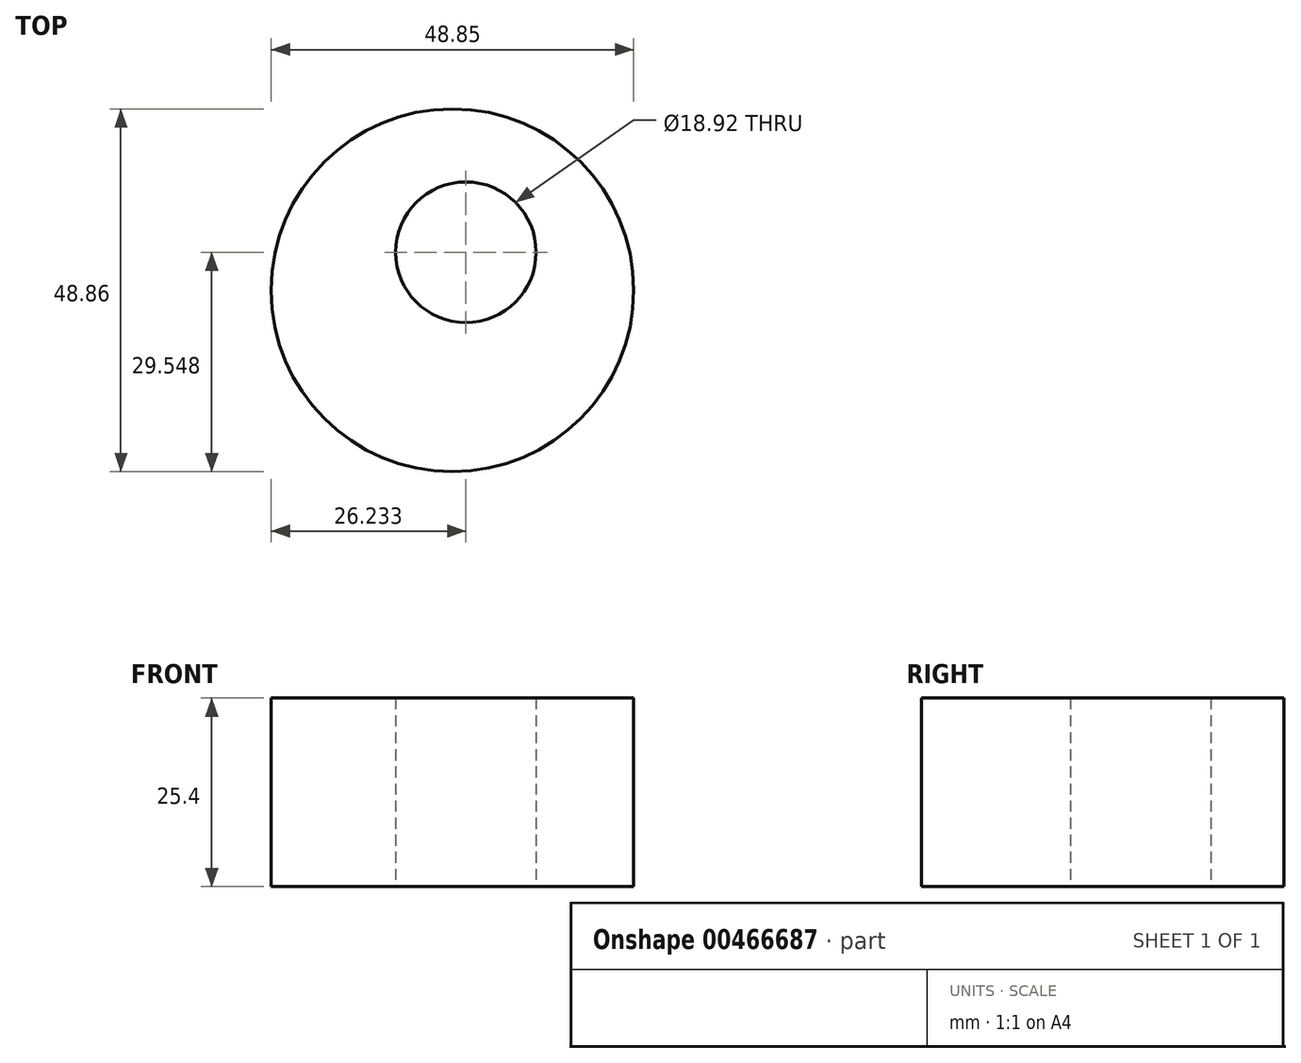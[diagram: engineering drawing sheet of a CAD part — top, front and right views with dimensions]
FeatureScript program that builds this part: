
annotation { "Feature Type Name" : "Feature", "Feature Type Description" : "" }
export const myFeature = defineFeature(function(context is Context, id is Id, definition is map)
    precondition{}
    {
        {
            var Q0;
            Q0=qCreatedBy(makeId("Top.planeOp"),FACE);
            var sketch = newSketch(context, id + "F0", { "sketchPlane" : qUnion([Q0])});
            skCircle(sketch, "E0", {"center": v(-11.27, 16.87) * mm, "radius": 24.43 * mm});
            skCircle(sketch, "E1", {"center": v(-9.47, 21.99) * mm, "radius": 9.46 * mm});
            skSolve(sketch);
        }
        {
            var Q0;
            Q0=makeQuery(id+"F0.imprint","IMPRINT",FACE,{"disambiguationData":[TD([[makeQuery(id+"F0.imprint","IMPRINT",EDGE,{"derivedFrom":sQuery(id+"F0.wireOp",EDGE,"E0")}),1.0]])]});
            extrude(context, id + "F1", {"entities" : qUnion([Q0]), "depth" : 25.4 * mm});
        }
    });
